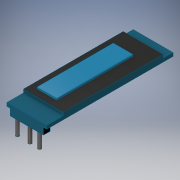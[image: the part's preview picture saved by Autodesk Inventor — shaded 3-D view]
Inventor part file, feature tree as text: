
AUTODESK INVENTOR PART (.ipt)
format: ipt  version: 2017.2 (Build 212223000, 223)  size: 158,720 bytes
history: native  units: in
note: dims shown in document units (in); Inventor stores cm internally (conversion verified against a paired STEP export)
features: sketch x7, extrude x5
ambient origin geometry x8: Origin, YZ Plane, XZ Plane, XY Plane, X Axis, Y Axis, Z Axis, Center Point
bodies: Solid1 (feature_tree)
feature tree (12):
  extrude  "Extrusion1"  Depth=0.4724in
  sketch  "Sketch2"  dims[d2=0.0394in d3=0.0in d4=1.1811in]
  extrude  "Extrusion2"  Depth=1.1811in
  sketch  "Sketch4"  dims[d5=0.4724in d6=0.0394in d7=0.0in]
  sketch  "Sketch5"  dims[d11=0.1969in d12=0.0787in]
  extrude  "Extrusion3"  Depth=0.0394in TaperAngle=0.0deg
  extrude  "Extrusion4"  Depth=0.0787in
  extrude  "Extrusion5"  Depth=0.0787in TaperAngle=0.0deg
  sketch  "Sketch1"  dims[d0=1.4961in d1=0.4724in]
  sketch  "Sketch6"  dims[d13=0.1969in d14=0.0787in d15=0.0in]
  sketch  "Sketch7"  dims[d16=0.0394in]
  sketch  "Sketch8"  dims[d17=0.0394in d18=0.0394in d19=0.1969in d20=0.0in d31=0.9055in d32=0.2362in d33=0.0197in d34=0.0in]
